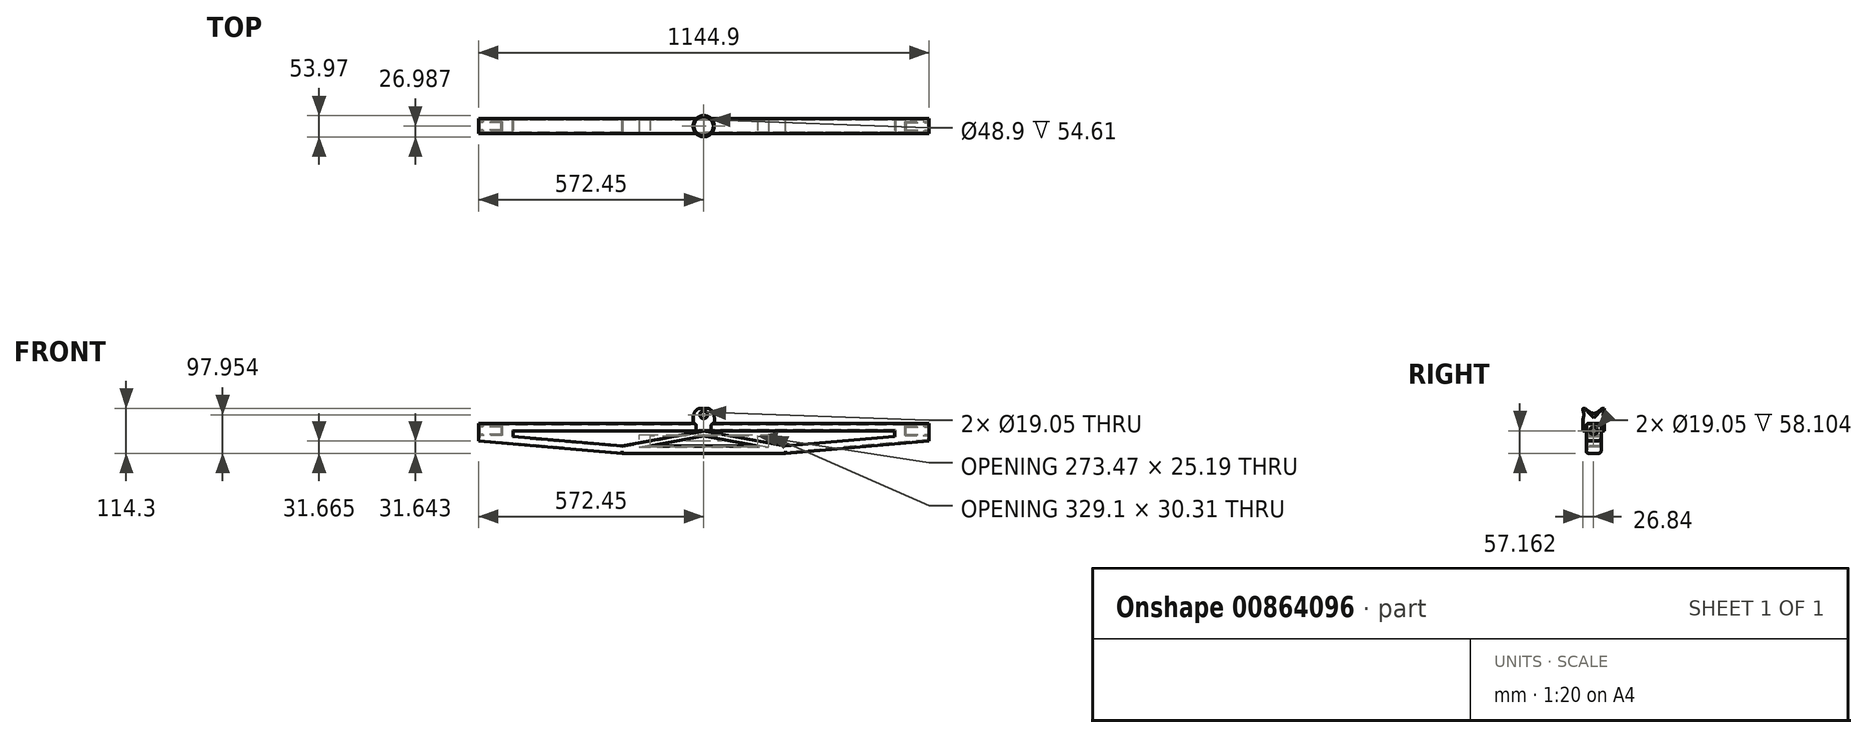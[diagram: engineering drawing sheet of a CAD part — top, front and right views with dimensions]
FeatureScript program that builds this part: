
annotation { "Feature Type Name" : "Feature", "Feature Type Description" : "" }
export const myFeature = defineFeature(function(context is Context, id is Id, definition is map)
    precondition{}
    {
        {
            var Q0;
            Q0=qCreatedBy(makeId("Front.planeOp"),FACE);
            var sketch = newSketch(context, id + "F0", { "sketchPlane" : qUnion([Q0])});
            skLineSegment(sketch, "E0", {"start": v(-207.68, 0) * mm, "end": v(-641.35, 0) * mm, "construction": true});
            skLineSegment(sketch, "E1", {"start": v(207.68, 0) * mm, "end": v(641.35, 0) * mm, "construction": true});
            skLineSegment(sketch, "E2.0", {"start": v(0, 76.2) * mm, "end": v(-641.35, 76.2) * mm});
            skLineSegment(sketch, "E2.1", {"start": v(0, 76.2) * mm, "end": v(641.35, 76.2) * mm});
            skLineSegment(sketch, "E3", {"start": v(-641.35, 76.2) * mm, "end": v(-641.35, 38.1) * mm});
            skLineSegment(sketch, "E4", {"start": v(-641.35, 38.1) * mm, "end": v(-207.68, 0) * mm});
            skLineSegment(sketch, "E5.MirrorCS", {"start": v(641.35, 38.1) * mm, "end": v(207.68, 0) * mm});
            skLineSegment(sketch, "E6.MirrorCS", {"start": v(641.35, 76.2) * mm, "end": v(641.35, 38.1) * mm});
            skLineSegment(sketch, "E7", {"start": v(-207.68, 0) * mm, "end": v(207.68, 0) * mm});
            skSolve(sketch);
        }
        {
            var Q0;
            Q0=makeQuery(id+"F0.imprint","IMPRINT",FACE,{"disambiguationData":[TD([[makeQuery(id+"F0.imprint","IMPRINT",EDGE,{"derivedFrom":sQuery(id+"F0.wireOp",EDGE,"E2.0")}),1.0]])]});
            extrude(context, id + "F1", {"entities" : qUnion([Q0]), "depth" : 38.1 * mm, "offsetDistance" : 25.4 * mm});
        }
        {
            var Q0;
            Q0=makeQuery(id+"F1.opExtrude","CAP_FACE",FACE,{"disambiguationData":[OSD([sQuery(id+"F0.wireOp",EDGE,"E2.0"),sQuery(id+"F0.wireOp",EDGE,"E2.1"),sQuery(id+"F0.wireOp",EDGE,"E3"),sQuery(id+"F0.wireOp",EDGE,"E4"),sQuery(id+"F0.wireOp",EDGE,"E5.MirrorCS"),sQuery(id+"F0.wireOp",EDGE,"E6.MirrorCS"),sQuery(id+"F0.wireOp",EDGE,"E7")])],"isStart":false});
            var sketch = newSketch(context, id + "F2", { "sketchPlane" : qUnion([Q0])});
            skLineSegment(sketch, "E8.0", {"start": v(-622.3, 57.15) * mm, "end": v(-622.3, 55.55) * mm});
            skLineSegment(sketch, "E8.1", {"start": v(-206.84, 19.05) * mm, "end": v(136.74, 19.05) * mm});
            skLineSegment(sketch, "E8.2", {"start": v(622.3, 55.55) * mm, "end": v(484.87, 43.48) * mm});
            skLineSegment(sketch, "E8.3", {"start": v(-622.3, 55.55) * mm, "end": v(-206.84, 19.05) * mm});
            skLineSegment(sketch, "E8.4", {"start": v(622.3, 57.15) * mm, "end": v(622.3, 55.55) * mm});
            skLineSegment(sketch, "E8.5", {"start": v(-622.3, 57.15) * mm, "end": v(0, 57.15) * mm});
            skLineSegment(sketch, "E9", {"start": v(-206.84, 19.05) * mm, "end": v(0, 57.15) * mm});
            skLineSegment(sketch, "E10.0", {"start": v(-136.74, 19.05) * mm, "end": v(0, 44.24) * mm});
            skLineSegment(sketch, "E11.0", {"start": v(0, 44.24) * mm, "end": v(136.74, 19.05) * mm});
            skLineSegment(sketch, "E12", {"start": v(-484.87, 57.15) * mm, "end": v(-484.87, 43.48) * mm});
            skLineSegment(sketch, "E13.trimOffspring", {"start": v(484.87, 57.15) * mm, "end": v(622.3, 57.15) * mm});
            skLineSegment(sketch, "E14.MirrorCS", {"start": v(206.84, 19.05) * mm, "end": v(0, 57.15) * mm});
            skLineSegment(sketch, "E15.MirrorCS", {"start": v(622.3, 57.15) * mm, "end": v(0, 57.15) * mm});
            skLineSegment(sketch, "E16.MirrorCS", {"start": v(622.3, 55.55) * mm, "end": v(206.84, 19.05) * mm});
            skLineSegment(sketch, "E17.MirrorCS", {"start": v(484.87, 57.15) * mm, "end": v(484.87, 43.48) * mm});
            skLineSegment(sketch, "E18", {"start": v(0, 57.15) * mm, "end": v(0, 57.15) * mm});
            skPoint(sketch, "E19.orphan", {"position": v(0, 57.15) * mm});
            skSolve(sketch);
        }
        {
            var Q0;
            {var subQ2=sQuery(id+"F2.wireOp",EDGE,"E9");Q0=makeQuery(id+"F2.imprint","IMPRINT",FACE,{"disambiguationData":[TD([[makeQuery(id+"F2.imprint","IMPRINT",EDGE,{"derivedFrom":subQ2}),1.0]])]});}
            var Q1;
            {var subQ0=sQuery(id+"F2.wireOp",EDGE,"E10.0");Q1=makeQuery(id+"F2.imprint","IMPRINT",FACE,{"disambiguationData":[TD([[makeQuery(id+"F2.imprint","IMPRINT",EDGE,{"derivedFrom":subQ0}),-1.0]])]});}
            extrude(context, id + "F3", {"entities" : qUnion([Q0, Q1]), "operationType" : NewBodyOperationType.REMOVE, "endBound" : BoundingType.THROUGH_ALL, "oppositeDirection" : true, "depth" : 25.4 * mm, "offsetDistance" : 25.4 * mm});
        }
        {
            var Q0;
            Q0=makeQuery(id+"F2.imprint","IMPRINT",FACE,{"disambiguationData":[TD([[makeQuery(id+"F2.imprint","IMPRINT",EDGE,{"derivedFrom":sQuery(id+"F2.wireOp",EDGE,"E14.MirrorCS")}),-1.0]])]});
            extrude(context, id + "F4", {"entities" : qUnion([Q0]), "operationType" : NewBodyOperationType.REMOVE, "endBound" : BoundingType.THROUGH_ALL, "oppositeDirection" : true, "depth" : 25.4 * mm, "offsetDistance" : 25.4 * mm});
        }
        {
            var Q0;
            Q0=makeQuery(id+"F1.opExtrude","CAP_EDGE",EDGE,{"disambiguationData":[OSD([sQuery(id+"F0.wireOp",EDGE,"E2.0"),sQuery(id+"F0.wireOp",EDGE,"E2.1")])],"isStart":true});
            var Q1;
            Q1=makeQuery(id+"F1.opExtrude","CAP_EDGE",EDGE,{"disambiguationData":[OSD([sQuery(id+"F0.wireOp",EDGE,"E2.0"),sQuery(id+"F0.wireOp",EDGE,"E2.1")])],"isStart":false});
            var Q2;
            Q2=makeQuery(id+"F1.opExtrude","CAP_EDGE",EDGE,{"disambiguationData":[OSD([sQuery(id+"F0.wireOp",EDGE,"E5.MirrorCS")])],"isStart":true});
            var Q3;
            Q3=makeQuery(id+"F1.opExtrude","CAP_EDGE",EDGE,{"disambiguationData":[OSD([sQuery(id+"F0.wireOp",EDGE,"E7")])],"isStart":true});
            var Q4;
            Q4=makeQuery(id+"F1.opExtrude","CAP_EDGE",EDGE,{"disambiguationData":[OSD([sQuery(id+"F0.wireOp",EDGE,"E4")])],"isStart":false});
            var Q5;
            Q5=makeQuery(id+"F1.opExtrude","CAP_EDGE",EDGE,{"disambiguationData":[OSD([sQuery(id+"F0.wireOp",EDGE,"E4")])],"isStart":true});
            var Q6;
            Q6=makeQuery(id+"F1.opExtrude","CAP_EDGE",EDGE,{"disambiguationData":[OSD([sQuery(id+"F0.wireOp",EDGE,"E7")])],"isStart":false});
            var Q7;
            Q7=makeQuery(id+"F1.opExtrude","CAP_EDGE",EDGE,{"disambiguationData":[OSD([sQuery(id+"F0.wireOp",EDGE,"E5.MirrorCS")])],"isStart":false});
            fillet(context, id + "F5", {"entities" : qUnion([Q0, Q1, Q2, Q3, Q4, Q5, Q6, Q7]), "radius" : 6.35 * mm, "tangentPropagation" : true, "allowEdgeOverflow" : false});
        }
        {
            var Q0;
            Q0=makeQuery(id+"F1.opExtrude","SWEPT_FACE",FACE,{"disambiguationData":[OSD([sQuery(id+"F0.wireOp",EDGE,"E6.MirrorCS")])]});
            var sketch = newSketch(context, id + "F6", { "sketchPlane" : qUnion([Q0])});
            skCircle(sketch, "E20", {"center": v(-19.05, 57.16) * mm, "radius": 9.53 * mm});
            skPoint(sketch, "E20.centerSnap0", {"position": v(-38.1, 57.16) * mm});
            skPoint(sketch, "E20.centerSnap1", {"position": v(-19.05, 76.2) * mm});
            skSolve(sketch);
        }
        {
            var Q0;
            Q0=makeQuery(id+"F6.imprint","IMPRINT",FACE,{"disambiguationData":[TD([[makeQuery(id+"F6.imprint","IMPRINT",EDGE,{"derivedFrom":sQuery(id+"F6.wireOp",EDGE,"E20")}),1.0]])]});
            extrude(context, id + "F7", {"entities" : qUnion([Q0]), "operationType" : NewBodyOperationType.REMOVE, "oppositeDirection" : true, "depth" : 50.8 * mm, "offsetDistance" : 25.4 * mm});
        }
        {
            var Q0;
            Q0=makeQuery(id+"F1.opExtrude","SWEPT_FACE",FACE,{"disambiguationData":[OSD([sQuery(id+"F0.wireOp",EDGE,"E3")])]});
            var sketch = newSketch(context, id + "F8", { "sketchPlane" : qUnion([Q0])});
            skCircle(sketch, "E21", {"center": v(19.05, 57.16) * mm, "radius": 9.53 * mm});
            skPoint(sketch, "E21.centerSnap0", {"position": v(0, 57.16) * mm});
            skPoint(sketch, "E21.centerSnap1", {"position": v(19.05, 76.2) * mm});
            skSolve(sketch);
        }
        {
            var Q0;
            Q0=makeQuery(id+"F8.imprint","IMPRINT",FACE,{"disambiguationData":[TD([[makeQuery(id+"F8.imprint","IMPRINT",EDGE,{"derivedFrom":sQuery(id+"F8.wireOp",EDGE,"E21")}),1.0]])]});
            extrude(context, id + "F9", {"entities" : qUnion([Q0]), "operationType" : NewBodyOperationType.REMOVE, "oppositeDirection" : true, "depth" : 50.8 * mm, "offsetDistance" : 25.4 * mm});
        }
        {
            var Q0;
            Q0=makeQuery(id+"F9.boolean.opBoolean","COPY",FACE,{"derivedFrom":makeQuery(id+"F9.opExtrude","CAP_FACE",FACE,{"disambiguationData":[OSD([sQuery(id+"F8.wireOp",EDGE,"E21")])],"isStart":false})});
            extrude(context, id + "F10", {"entities" : qUnion([Q0]), "operationType" : NewBodyOperationType.REMOVE, "oppositeDirection" : true, "depth" : 76.2 * mm, "offsetDistance" : 25.4 * mm});
        }
        {
            var Q0;
            Q0=makeQuery(id+"F7.boolean.opBoolean","COPY",FACE,{"derivedFrom":makeQuery(id+"F7.opExtrude","CAP_FACE",FACE,{"disambiguationData":[OSD([sQuery(id+"F6.wireOp",EDGE,"E20")])],"isStart":false})});
            extrude(context, id + "F11", {"entities" : qUnion([Q0]), "operationType" : NewBodyOperationType.REMOVE, "oppositeDirection" : true, "depth" : 76.2 * mm, "offsetDistance" : 25.4 * mm});
        }
        {
            var Q0;
            Q0=qCreatedBy(makeId("Front.planeOp"),FACE);
            var sketch = newSketch(context, id + "F12", { "sketchPlane" : qUnion([Q0])});
            skLineSegment(sketch, "E22.bottom", {"start": v(-572.45, -27.1) * mm, "end": v(-641.6, -27.1) * mm});
            skLineSegment(sketch, "E22.top", {"start": v(-572.45, 134.76) * mm, "end": v(-641.6, 134.76) * mm});
            skLineSegment(sketch, "E22.left", {"start": v(-572.45, -27.1) * mm, "end": v(-572.45, 134.76) * mm});
            skLineSegment(sketch, "E22.right", {"start": v(-641.6, -27.1) * mm, "end": v(-641.6, 134.76) * mm});
            skPoint(sketch, "E22.middle", {"position": v(-607.02, 53.83) * mm});
            skLineSegment(sketch, "E23.MirrorCS", {"start": v(572.45, -27.1) * mm, "end": v(572.45, 134.76) * mm});
            skLineSegment(sketch, "E24.MirrorCS", {"start": v(572.45, -27.1) * mm, "end": v(641.6, -27.1) * mm});
            skLineSegment(sketch, "E25.MirrorCS", {"start": v(641.6, -27.1) * mm, "end": v(641.6, 134.76) * mm});
            skLineSegment(sketch, "E26.MirrorCS", {"start": v(572.45, 134.76) * mm, "end": v(641.6, 134.76) * mm});
            skSolve(sketch);
        }
        {
            var Q0;
            Q0=makeQuery(id+"F12.imprint","IMPRINT",FACE,{"disambiguationData":[TD([[makeQuery(id+"F12.imprint","IMPRINT",EDGE,{"derivedFrom":sQuery(id+"F12.wireOp",EDGE,"E22.bottom")}),-1.0]])]});
            var Q1;
            Q1=makeQuery(id+"F12.imprint","IMPRINT",FACE,{"disambiguationData":[TD([[makeQuery(id+"F12.imprint","IMPRINT",EDGE,{"derivedFrom":sQuery(id+"F12.wireOp",EDGE,"E23.MirrorCS")}),-1.0]])]});
            extrude(context, id + "F13", {"entities" : qUnion([Q0, Q1]), "operationType" : NewBodyOperationType.REMOVE, "depth" : 101.6 * mm, "offsetDistance" : 25.4 * mm, "symmetric" : true});
        }
        {
            var Q0;
            Q0=makeQuery(id+"F1.opExtrude","SWEPT_FACE",FACE,{"disambiguationData":[OSD([sQuery(id+"F0.wireOp",EDGE,"E2.0"),sQuery(id+"F0.wireOp",EDGE,"E2.1")])]});
            var sketch = newSketch(context, id + "F14", { "sketchPlane" : qUnion([Q0])});
            skLineSegment(sketch, "E27", {"start": v(-572.45, -19.05) * mm, "end": v(572.45, -19.05) * mm, "construction": true});
            skSolve(sketch);
        }
        {
            var Q0;
            {var subQ0=sQuery(id+"F0.wireOp",EDGE,"E2.1");var subQ1=sQuery(id+"F0.wireOp",EDGE,"E2.0");var subQ2=makeQuery(id+"F1.opExtrude","SWEPT_FACE",FACE,{"disambiguationData":[OSD([subQ1,subQ0])]});var subQ3=subQ2;Q0=makeQuery(id+"F14.imprint","IMPRINT",FACE,{"disambiguationData":[TD([[makeQuery(id+"F14.imprint","IMPRINT",EDGE,{"derivedFrom":makeQuery(id+"F13.boolean.opBoolean","INTERSECT",EDGE,{"derivedFrom":[subQ3,makeQuery(id+"F13.opExtrude","SWEPT_FACE",FACE,{"disambiguationData":[OSD([sQuery(id+"F12.wireOp",EDGE,"E22.left")])]})]})}),1.0]])]});}
            var sketch = newSketch(context, id + "F15", { "sketchPlane" : qUnion([Q0])});
            skCircle(sketch, "E28", {"center": v(0, -18.9) * mm, "radius": 26.99 * mm});
            skSolve(sketch);
        }
        {
            var Q0;
            Q0 = qSketchRegion(id + "F15", true);
            extrude(context, id + "F16", {"entities" : qUnion([Q0]), "operationType" : NewBodyOperationType.ADD, "depth" : 38.1 * mm, "offsetDistance" : 25.4 * mm, "hasSecondDirection" : true, "secondDirectionOppositeDirection" : true, "secondDirectionDepth" : 19.05 * mm});
        }
        {
            var Q0;
            Q0=makeQuery(id+"F16.opExtrude","CAP_FACE",FACE,{"disambiguationData":[OSD([sQuery(id+"F15.wireOp",EDGE,"E28")])],"isStart":false});
            shell(context, id + "F17", {"entities" : qUnion([Q0]), "thickness" : 2.54 * mm});
        }
        {
            var Q0;
            Q0=qCreatedBy(makeId("Front.planeOp"),FACE);
            var sketch = newSketch(context, id + "F18", { "sketchPlane" : qUnion([Q0])});
            skCircle(sketch, "E29", {"center": v(0, 90.24) * mm, "radius": 26.99 * mm});
            skLineSegment(sketch, "E30", {"start": v(-42.43, 90.24) * mm, "end": v(48.04, 90.24) * mm});
            skLineSegment(sketch, "E31", {"start": v(48.04, 90.24) * mm, "end": v(48.04, 134.43) * mm});
            skLineSegment(sketch, "E32", {"start": v(48.04, 134.43) * mm, "end": v(-43.13, 134.43) * mm});
            skLineSegment(sketch, "E33", {"start": v(-43.13, 134.43) * mm, "end": v(-42.43, 90.24) * mm});
            skSolve(sketch);
        }
        {
            var Q0;
            {var subQ0=sQuery(id+"F18.wireOp",EDGE,"E31");Q0=makeQuery(id+"F18.imprint","IMPRINT",FACE,{"disambiguationData":[TD([[makeQuery(id+"F18.imprint","IMPRINT",EDGE,{"derivedFrom":subQ0}),1.0]])]});}
            extrude(context, id + "F19", {"entities" : qUnion([Q0]), "operationType" : NewBodyOperationType.REMOVE, "oppositeDirection" : true, "depth" : 152.4 * mm, "offsetDistance" : 25.4 * mm, "symmetric" : true});
        }
        {
            var Q0;
            Q0=qCreatedBy(makeId("Front.planeOp"),FACE);
            var sketch = newSketch(context, id + "F20", { "sketchPlane" : qUnion([Q0])});
            skCircle(sketch, "E34", {"center": v(0, 97.95) * mm, "radius": 9.53 * mm});
            skSolve(sketch);
        }
        {
            var Q0;
            Q0=makeQuery(id+"F20.imprint","IMPRINT",FACE,{"disambiguationData":[TD([[makeQuery(id+"F20.imprint","IMPRINT",EDGE,{"derivedFrom":sQuery(id+"F20.wireOp",EDGE,"E34")}),1.0]])]});
            extrude(context, id + "F21", {"entities" : qUnion([Q0]), "operationType" : NewBodyOperationType.REMOVE, "oppositeDirection" : true, "depth" : 101.6 * mm, "offsetDistance" : 25.4 * mm, "symmetric" : true});
        }
    });
